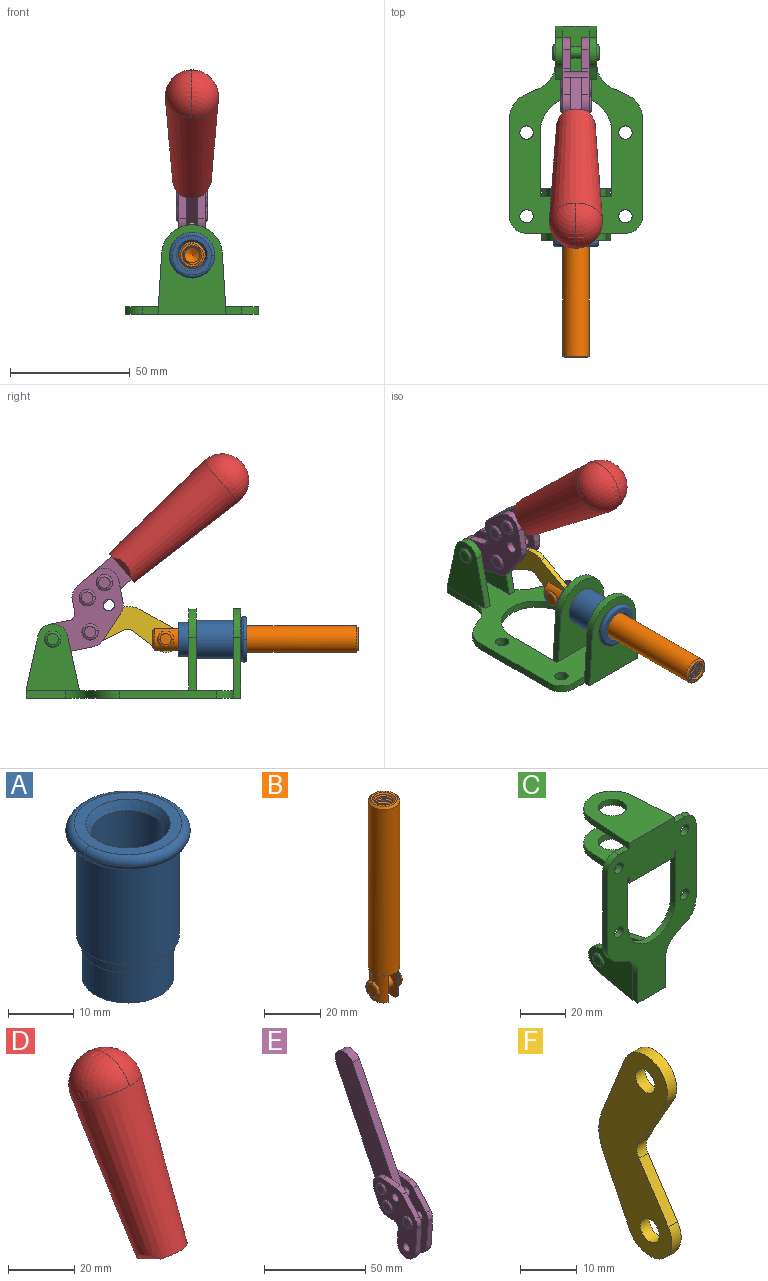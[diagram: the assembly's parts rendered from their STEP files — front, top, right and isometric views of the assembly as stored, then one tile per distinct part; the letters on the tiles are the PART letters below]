
ASSEMBLY  parts=6 mates=6
PART A: 15 faces, bbox 20.6x20.6x28.7 mm
  f0: torus R=8.26mm, axis (0,0,1), area 56.8mm2, adj f1,f10,f12
  f1: torus R=8.26mm, axis (0,0,1), area 56.8mm2, adj f0,f6,f13
  f2: cylinder r=5.59mm len=25.91mm, axis (0,0,1), area 909.6mm2, adj f3,f4
  f3: cone r=6.86mm half-angle=45deg, axis (0,0,-1), area 70.2mm2, adj f2,f14
  f4: cone r=6.47mm half-angle=30deg, axis (0,0,1), area 66.7mm2, adj f2,f13
  f5: cylinder r=7.04mm len=14.07mm, axis (0,0,1), area 252.6mm2, adj f11,f14
  f6: torus R=8.26mm, axis (0,0,1), area 56.8mm2, adj f1,f12,f13
  f7: cylinder r=7.16mm len=14.33mm, axis (0,0,1), area 91.5mm2, adj f9,f11
  f8: cylinder r=7.86mm len=18.42mm, axis (0,0,1), area 909.6mm2, adj f9,f10
  f9: plane 15.72x15.72mm, normal (0,0,-1), area 33mm2, adj f7,f8
  f10: plane 16.51x16.51mm, normal (0,0,-1), area 19.9mm2, adj f0,f8,f12
  f11: plane 14.33x14.33mm, normal (0,0,-1), area 5.7mm2, adj f5,f7
  f12: torus R=8.26mm, axis (0,0,1), area 56.8mm2, adj f0,f6,f10
  f13: plane 16.51x16.51mm, normal (0,0,1), area 82.7mm2, adj f1,f4,f6
  f14: plane 14.07x14.07mm, normal (0,0,-1), area 7.8mm2, adj f3,f5
PART B: 48 faces, bbox 12.6x11.1x86.1 mm
  f0: torus R=2.41mm, axis (-1,0,0), area 15mm2, adj f30,f32,f34
  f1: torus R=2.41mm, axis (-1,0,0), area 15mm2, adj f29,f31,f33
  f2: cylinder r=5.54mm len=72.39mm, axis (0,0,1), area 2518.5mm2, adj f3,f4,f42,f43
  f3: cone r=5.54mm half-angle=45deg, axis (0,0,1), area 7.6mm2, adj f2,f5,f41
  f4: cone r=5.54mm half-angle=45deg, axis (0,0,-1), area 34.9mm2, adj f2,f39
  f5: cylinder r=5.08mm len=11.48mm, axis (0,0,1), area 108.3mm2, adj f3,f7,f8,f41
  f6: cylinder r=2.41mm len=4.83mm, axis (-1,0,0), area 71.2mm2, adj f40,f41
  f7: cylinder r=2.41mm len=4.83mm, axis (-1,0,0), area 7.6mm2, adj f5,f34
  f8: cone r=5.08mm half-angle=45deg, axis (0,0,1), area 10.6mm2, adj f5,f37,f41
  f9: cone r=3.98mm half-angle=45deg, axis (0,0,1), area 17.6mm2, adj f27,f39,f45,f46,f47
  f10: cylinder r=2.41mm len=4.83mm, axis (-1,0,0), area 7.6mm2, adj f33,f38
  f11: cylinder r=3.2mm len=6.4mm, axis (0,0,1), area 78.4mm2, adj f12,f28,f44,f45,f47
  f12: cylinder r=3.2mm len=6.4mm, axis (0,0,1), area 10.5mm2, adj f11,f13,f45,f47
  f13: cylinder r=3.2mm len=6.4mm, axis (0,0,1), area 10.5mm2, adj f12,f14,f45,f47
  f14: cylinder r=3.2mm len=6.4mm, axis (0,0,1), area 10.5mm2, adj f13,f15,f45,f47
  f15: cylinder r=3.2mm len=6.4mm, axis (0,0,1), area 10.5mm2, adj f14,f16,f45,f47
  f16: cylinder r=3.2mm len=6.4mm, axis (0,0,1), area 10.5mm2, adj f15,f17,f45,f47
  f17: cylinder r=3.2mm len=6.4mm, axis (0,0,1), area 10.5mm2, adj f16,f18,f45,f47
  f18: cylinder r=3.2mm len=6.4mm, axis (0,0,1), area 10.5mm2, adj f17,f19,f45,f47
  f19: cylinder r=3.2mm len=6.4mm, axis (0,0,1), area 10.5mm2, adj f18,f20,f45,f47
  f20: cylinder r=3.2mm len=6.4mm, axis (0,0,1), area 10.5mm2, adj f19,f21,f45,f47
  f21: cylinder r=3.2mm len=6.4mm, axis (0,0,1), area 10.5mm2, adj f20,f22,f45,f47
  f22: cylinder r=3.2mm len=6.4mm, axis (0,0,1), area 10.5mm2, adj f21,f23,f45,f47
  f23: cylinder r=3.2mm len=6.4mm, axis (0,0,1), area 10.5mm2, adj f22,f24,f45,f47
  f24: cylinder r=3.2mm len=6.4mm, axis (0,0,1), area 10.5mm2, adj f23,f25,f45,f47
  f25: cylinder r=3.2mm len=6.4mm, axis (0,0,1), area 10.5mm2, adj f24,f26,f45,f47
  f26: cylinder r=3.2mm len=6.4mm, axis (0,0,1), area 10.5mm2, adj f25,f27,f45,f47
  f27: cylinder r=3.2mm len=6.4mm, axis (0,0,1), area 7.4mm2, adj f9,f26,f45,f47
  f28: cone r=3.2mm half-angle=60deg, axis (0,0,1), area 37.2mm2, adj f11
  f29: plane 4.83x4.83mm, normal (-1,0,0), area 18.3mm2, adj f1,f31
  f30: plane 4.83x4.83mm, normal (1,0,0), area 18.3mm2, adj f0,f32
  f31: torus R=2.41mm, axis (-1,0,0), area 15mm2, adj f1,f29,f33
  f32: torus R=2.41mm, axis (-1,0,0), area 15mm2, adj f0,f30,f34
  f33: plane 6.83x6.83mm, normal (1,0,0), area 18.3mm2, adj f1,f10,f31
  f34: plane 6.83x6.83mm, normal (-1,0,0), area 18.3mm2, adj f0,f7,f32
  f35: cone r=5.08mm half-angle=45deg, axis (0,0,1), area 10.6mm2, adj f36,f38,f40
  f36: plane 7.25x1.97mm, normal (0,0,-1), area 10mm2, adj f35,f40
  f37: plane 7.25x1.97mm, normal (0,0,-1), area 10mm2, adj f8,f41
  f38: cylinder r=5.08mm len=11.48mm, axis (0,0,1), area 108.3mm2, adj f10,f35,f40,f42
  f39: plane 9.55x9.55mm, normal (0,0,1), area 22mm2, adj f4,f9
  f40: plane 12.76x10.09mm, normal (1,0,0), area 95.7mm2, adj f6,f35,f36,f38,f42,f43
  f41: plane 12.76x10.09mm, normal (-1,0,0), area 95.7mm2, adj f3,f5,f6,f8,f37,f43
  f42: cone r=5.54mm half-angle=45deg, axis (0,0,1), area 7.6mm2, adj f2,f38,f40
  f43: plane 11.07x4.7mm, normal (0,0,-1), area 50.4mm2, adj f2,f40,f41
  f44: plane 0.89x0.62mm, normal (-1,0,0), area 0.3mm2, adj f11,f45,f46,f47
  f45: bspline ~24.8x7.63mm, area 266.6mm2, adj f9,f11,f12,f13,f14,f15,f16,f17
  f46: bspline ~24.87x7.63mm, area 73.6mm2, adj f9,f44,f45,f47
  f47: bspline ~24.98x7.63mm, area 272.5mm2, adj f9,f11,f12,f13,f14,f15,f16,f17
PART C: 55 faces, bbox 55.7x37.4x89.8 mm
  f0: torus R=2.41mm, axis (-1,0,0), area 15mm2, adj f11,f15,f25
  f1: torus R=2.41mm, axis (-1,0,0), area 15mm2, adj f10,f12,f22
  f2: cylinder r=2.78mm len=5.56mm, axis (0,-1,0), area 54.2mm2, adj f30,f54
  f3: cylinder r=14.99mm len=29.97mm, axis (0,-1,0), area 145.9mm2, adj f30,f49,f53,f54
  f4: cylinder r=2.78mm len=5.56mm, axis (0,-1,0), area 54.2mm2, adj f30,f54
  f5: cylinder r=2.78mm len=5.56mm, axis (0,-1,0), area 54.2mm2, adj f30,f54
  f6: cylinder r=2.78mm len=5.56mm, axis (0,-1,0), area 54.2mm2, adj f30,f54
  f7: cylinder r=6.35mm len=12.7mm, axis (0,0,1), area 123.6mm2, adj f27,f51
  f8: cylinder r=6.35mm len=12.7mm, axis (0,0,-1), area 124.7mm2, adj f21,f35
  f9: cylinder r=2.41mm len=11.18mm, axis (-1,0,0), area 169.4mm2, adj f16,f19
  f10: plane 4.83x4.83mm, normal (1,0,0), area 18.3mm2, adj f1,f12
  f11: plane 4.83x4.83mm, normal (-1,0,0), area 18.3mm2, adj f0,f15
  f12: torus R=2.41mm, axis (-1,0,0), area 15mm2, adj f1,f10,f22
  f13: cylinder r=6.35mm len=12.41mm, axis (1,0,0), area 53.4mm2, adj f18,f19,f22,f23
  f14: cylinder r=6.35mm len=12.41mm, axis (-1,0,0), area 53.4mm2, adj f16,f17,f24,f25
  f15: torus R=2.41mm, axis (-1,0,0), area 15mm2, adj f0,f11,f25
  f16: plane 27.86x22.35mm, normal (1,0,0), area 425.4mm2, adj f9,f14,f17,f24,f30
  f17: plane 22.86x4.97mm, normal (0,0.21,0.98), area 72.5mm2, adj f14,f16,f25,f30
  f18: plane 22.86x4.97mm, normal (0,0.21,0.98), area 72.5mm2, adj f13,f19,f22,f30
  f19: plane 27.86x22.35mm, normal (-1,0,0), area 425.4mm2, adj f9,f13,f18,f23,f30
  f20: cylinder r=12.7mm len=25.35mm, axis (0,0,-1), area 119.8mm2, adj f21,f34,f35,f36
  f21: plane 34.21x28.07mm, normal (0,0,-1), area 702.4mm2, adj f8,f20,f30,f34,f36
  f22: plane 27.96x22.45mm, normal (1,0,0), area 407.2mm2, adj f1,f12,f13,f18,f23,f30,f42,f43
  f23: plane 22.86x4.97mm, normal (0,0.21,-0.98), area 72.5mm2, adj f13,f19,f22,f44
  f24: plane 22.86x4.97mm, normal (0,0.21,-0.98), area 72.5mm2, adj f14,f16,f25,f44
  f25: plane 27.86x22.35mm, normal (-1,0,0), area 407.1mm2, adj f0,f14,f15,f17,f24,f30,f45,f46
  f26: plane 3.1x0.95mm, normal (0,0,-1), area 2.7mm2, adj f30,f49,f50,f54
  f27: plane 34.21x28.07mm, normal (0,0,1), area 702.4mm2, adj f7,f28,f30,f50,f52
  f28: cylinder r=12.7mm len=25.35mm, axis (0,0,1), area 118.8mm2, adj f27,f50,f51,f52
  f29: plane 3.1x0.95mm, normal (0,0,-1), area 2.7mm2, adj f30,f52,f53,f54
  f30: plane 86.54x55.63mm, normal (0,1,0), area 2362.9mm2, adj f2,f3,f4,f5,f6,f16,f17,f18
  f31: plane 40.56x3.1mm, normal (-1,0,0), area 125.7mm2, adj f30,f32,f48,f54
  f32: cylinder r=7.11mm len=7.11mm, axis (0,-1,0), area 34.6mm2, adj f30,f31,f33,f54
  f33: plane 6.67x3.1mm, normal (0,0,1), area 20.4mm2, adj f30,f32,f34,f54
  f34: plane 25.39x3.13mm, normal (-1,0.06,0), area 79.5mm2, adj f20,f21,f33,f35,f54
  f35: plane 37.31x28.45mm, normal (0,0,1), area 789.9mm2, adj f8,f20,f34,f36,f54
  f36: plane 25.39x3.13mm, normal (1,0.06,0), area 79.5mm2, adj f20,f21,f35,f37,f54
  f37: plane 6.67x3.1mm, normal (0,0,1), area 20.4mm2, adj f30,f36,f38,f54
  f38: cylinder r=7.11mm len=7.11mm, axis (0,-1,0), area 34.6mm2, adj f30,f37,f39,f54
  f39: plane 40.56x3.1mm, normal (1,0,0), area 125.7mm2, adj f30,f38,f40,f54
  f40: cylinder r=11.18mm len=10.16mm, axis (0,-1,0), area 39.5mm2, adj f30,f39,f41,f54
  f41: plane 6.09x3.1mm, normal (0.42,0,-0.91), area 20.8mm2, adj f30,f40,f42,f54
  f42: cylinder r=11.18mm len=9.41mm, axis (0,-1,0), area 37.2mm2, adj f22,f30,f41,f43,f54
  f43: plane 16.5x3.1mm, normal (1,0,0), area 51.1mm2, adj f22,f42,f44,f54
  f44: plane 17.37x3.1mm, normal (0,0,-1), area 53.8mm2, adj f23,f24,f30,f43,f45,f54
  f45: plane 16.5x3.1mm, normal (-1,0,0), area 51.1mm2, adj f25,f44,f46,f54
  f46: cylinder r=11.18mm len=9.41mm, axis (0,-1,0), area 37.2mm2, adj f25,f30,f45,f47,f54
  f47: plane 6.09x3.1mm, normal (-0.42,0,-0.91), area 20.8mm2, adj f30,f46,f48,f54
  f48: cylinder r=11.18mm len=10.16mm, axis (0,-1,0), area 39.5mm2, adj f30,f31,f47,f54
  f49: plane 26.54x3.1mm, normal (-1,0,0), area 82.3mm2, adj f3,f26,f30,f54
  f50: plane 25.39x3.1mm, normal (1,0.06,0), area 78.8mm2, adj f26,f27,f28,f51,f54
  f51: plane 37.31x28.45mm, normal (0,0,-1), area 789.9mm2, adj f7,f28,f50,f52,f54
  f52: plane 25.39x3.1mm, normal (-1,0.06,0), area 78.8mm2, adj f27,f28,f29,f51,f54
  f53: plane 26.54x3.1mm, normal (1,0,0), area 82.3mm2, adj f3,f29,f30,f54
  f54: plane 89.66x55.63mm, normal (0,-1,0), area 2678.5mm2, adj f2,f3,f4,f5,f6,f26,f29,f31
PART D: 11 faces, bbox 22.3x42.6x64.5 mm
  f0: sphere r=11.13mm, area 411.4mm2, adj f1,f8
  f1: cone r=11.11mm half-angle=3.3deg, axis (0,0.44,0.9), area 3251.8mm2, adj f0,f7,f8,f9,f10
  f2: cylinder r=6.16mm len=11.7mm, axis (1,0,0), area 89.5mm2, adj f3,f4,f5,f6
  f3: plane 60.23x36.75mm, normal (-1,0,0), area 763.6mm2, adj f2,f4,f6,f10
  f4: plane 51.37x25.05mm, normal (0,0.9,-0.44), area 264.2mm2, adj f2,f3,f5,f10
  f5: plane 60.23x36.75mm, normal (1,0,0), area 763.6mm2, adj f2,f4,f6,f10
  f6: plane 51.37x25.05mm, normal (0,-0.9,0.44), area 264.2mm2, adj f2,f3,f5,f10
  f7: plane 9.95x5.95mm, normal (0.71,-0.31,-0.64), area 25.8mm2, adj f1,f10
  f8: sphere r=11.13mm, area 411.4mm2, adj f0,f1
  f9: plane 9.95x5.95mm, normal (-0.71,-0.31,-0.64), area 25.8mm2, adj f1,f10
  f10: plane 14.27x11.38mm, normal (0,-0.44,-0.9), area 106.7mm2, adj f1,f3,f4,f5,f6,f7,f9
PART E: 59 faces, bbox 12.9x60.2x99.6 mm
  f0: torus R=2.39mm, axis (-1,0,0), area 14.9mm2, adj f20,f43,f51
  f1: torus R=2.39mm, axis (-1,0,0), area 14.9mm2, adj f19,f42,f51
  f2: torus R=2.39mm, axis (-1,0,0), area 14.9mm2, adj f18,f35,f51
  f3: torus R=2.39mm, axis (-1,0,0), area 14.9mm2, adj f14,f17,f23
  f4: torus R=2.39mm, axis (-1,0,0), area 14.9mm2, adj f13,f16,f23
  f5: torus R=2.39mm, axis (-1,0,0), area 14.9mm2, adj f12,f15,f23
  f6: cylinder r=2.39mm len=4.78mm, axis (1,0,0), area 46.5mm2, adj f48,f50,f51
  f7: cylinder r=2.39mm len=4.78mm, axis (1,0,0), area 46.5mm2, adj f50,f51
  f8: cylinder r=6.35mm len=12.68mm, axis (1,0,0), area 61.8mm2, adj f38,f39,f50,f51
  f9: cylinder r=2.39mm len=4.78mm, axis (-1,0,0), area 70.5mm2, adj f46,f50
  f10: cylinder r=2.39mm len=4.78mm, axis (-1,0,0), area 46.5mm2, adj f23,f45,f46
  f11: cylinder r=2.39mm len=4.78mm, axis (-1,0,0), area 46.5mm2, adj f23,f46
  f12: plane 4.78x4.78mm, normal (1,0,0), area 17.9mm2, adj f5,f15
  f13: plane 4.78x4.78mm, normal (1,0,0), area 17.9mm2, adj f4,f16
  f14: plane 4.78x4.78mm, normal (1,0,0), area 17.9mm2, adj f3,f17
  f15: torus R=2.39mm, axis (-1,0,0), area 14.9mm2, adj f5,f12,f23
  f16: torus R=2.39mm, axis (-1,0,0), area 14.9mm2, adj f4,f13,f23
  f17: torus R=2.39mm, axis (-1,0,0), area 14.9mm2, adj f3,f14,f23
  f18: plane 4.78x4.78mm, normal (-1,0,0), area 17.9mm2, adj f2,f35
  f19: plane 4.78x4.78mm, normal (-1,0,0), area 17.9mm2, adj f1,f42
  f20: plane 4.78x4.78mm, normal (-1,0,0), area 17.9mm2, adj f0,f43
  f21: plane 2.26x0.2mm, normal (1,0,0), area 0.2mm2, adj f31,f44
  f22: plane 2.26x0.2mm, normal (-1,0,0), area 0.2mm2, adj f41,f44
  f23: plane 39.37x30.77mm, normal (1,0,0), area 565.5mm2, adj f3,f4,f5,f10,f11,f15,f16,f17
  f24: cylinder r=6.1mm len=4.15mm, axis (-1,0,0), area 14.7mm2, adj f23,f25,f32,f46
  f25: plane 10.25x9.01mm, normal (0,-0.75,0.66), area 42.3mm2, adj f23,f24,f26,f46
  f26: cylinder r=6.35mm len=4.64mm, axis (-1,0,0), area 15.6mm2, adj f23,f25,f27,f46
  f27: plane 15.84x3.1mm, normal (0,-1,-0.07), area 49.2mm2, adj f23,f26,f28,f46
  f28: cylinder r=6.35mm len=12.68mm, axis (-1,0,0), area 61.8mm2, adj f23,f27,f29,f46
  f29: plane 8.11x3.1mm, normal (0,1,0.07), area 25.2mm2, adj f23,f28,f30,f46
  f30: cylinder r=3.05mm len=3.25mm, axis (-1,0,0), area 14.8mm2, adj f23,f29,f31,f46
  f31: plane 5.99x3.1mm, normal (0,0.07,-1), area 18.6mm2, adj f21,f23,f30,f44,f46
  f32: plane 9.5x3.1mm, normal (0,-0.07,1), area 29.5mm2, adj f23,f24,f33,f46,f47
  f33: cylinder r=6.1mm len=8.63mm, axis (-1,0,0), area 39.1mm2, adj f23,f32,f34,f47
  f34: plane 8.65x3.96mm, normal (0,0.91,-0.42), area 29.5mm2, adj f23,f33,f44,f47
  f35: torus R=2.39mm, axis (-1,0,0), area 14.9mm2, adj f2,f18,f51
  f36: plane 10.25x9.01mm, normal (0,-0.75,0.66), area 42.3mm2, adj f37,f49,f50,f51
  f37: cylinder r=6.35mm len=4.64mm, axis (1,0,0), area 15.6mm2, adj f36,f38,f50,f51
  f38: plane 15.84x3.1mm, normal (0,-1,-0.07), area 49.2mm2, adj f8,f37,f50,f51
  f39: plane 8.11x3.1mm, normal (0,1,0.07), area 25.2mm2, adj f8,f40,f50,f51
  f40: cylinder r=3.05mm len=3.25mm, axis (1,0,0), area 14.8mm2, adj f39,f41,f50,f51
  f41: plane 5.99x3.1mm, normal (0,0.07,-1), area 18.6mm2, adj f22,f40,f44,f50,f51
  f42: torus R=2.39mm, axis (-1,0,0), area 14.9mm2, adj f1,f19,f51
  f43: torus R=2.39mm, axis (-1,0,0), area 14.9mm2, adj f0,f20,f51
  f44: cylinder r=6.35mm len=12.12mm, axis (-1,0,0), area 128.9mm2, adj f21,f22,f23,f31,f34,f41,f46,f47
  f45: plane 2.65x1.35mm, normal (1,0,0), area 1mm2, adj f10,f55
  f46: plane 39.08x20.42mm, normal (-1,0,0), area 412.5mm2, adj f9,f10,f11,f24,f25,f26,f27,f28
  f47: plane 77.62x39.82mm, normal (1,0,0), area 850mm2, adj f32,f33,f34,f44,f53,f54,f55
  f48: plane 2.65x1.35mm, normal (-1,0,0), area 1mm2, adj f6,f55
  f49: cylinder r=6.1mm len=4.15mm, axis (1,0,0), area 14.7mm2, adj f36,f50,f51,f56
  f50: plane 39.08x20.42mm, normal (1,0,0), area 412.5mm2, adj f6,f7,f8,f9,f36,f37,f38,f39
  f51: plane 39.37x30.77mm, normal (-1,0,0), area 565.5mm2, adj f0,f1,f2,f6,f7,f8,f35,f36
  f52: plane 8.65x3.96mm, normal (0,0.91,-0.42), area 29.5mm2, adj f44,f51,f57,f58
  f53: plane 68.49x33.4mm, normal (0,0.9,-0.44), area 358.1mm2, adj f44,f47,f54,f58
  f54: cylinder r=6.35mm len=12.06mm, axis (1,0,0), area 93.7mm2, adj f47,f53,f55,f58
  f55: plane 68.49x33.4mm, normal (0,-0.9,0.44), area 358.1mm2, adj f44,f45,f46,f47,f48,f50,f54,f58
  f56: plane 9.5x3.1mm, normal (0,-0.07,1), area 29.5mm2, adj f49,f50,f51,f57,f58
  f57: cylinder r=6.1mm len=8.63mm, axis (1,0,0), area 39.1mm2, adj f51,f52,f56,f58
  f58: plane 77.62x39.82mm, normal (-1,0,0), area 850mm2, adj f44,f52,f53,f54,f55,f56,f57
PART F: 12 faces, bbox 2.3x18.2x42.8 mm
  f0: cylinder r=2.4mm len=4.8mm, axis (1,0,0), area 34.9mm2, adj f4,f11
  f1: cylinder r=10.41mm len=8.47mm, axis (1,0,0), area 20.2mm2, adj f4,f9,f10,f11
  f2: cylinder r=3.05mm len=3.16mm, axis (1,0,0), area 7.7mm2, adj f4,f6,f7,f11
  f3: cylinder r=2.4mm len=4.8mm, axis (1,0,0), area 34.9mm2, adj f4,f11
  f4: plane 42.81x18.23mm, normal (-1,0,0), area 414.1mm2, adj f0,f1,f2,f3,f5,f6,f7,f8
  f5: cylinder r=5.54mm len=10.67mm, axis (1,0,0), area 41.8mm2, adj f4,f6,f10,f11
  f6: plane 11.66x6.53mm, normal (0,-0.87,-0.49), area 30.9mm2, adj f2,f4,f5,f11
  f7: plane 11.17x7.33mm, normal (0,-0.84,0.55), area 30.9mm2, adj f2,f4,f8,f11
  f8: cylinder r=5.54mm len=10.51mm, axis (1,0,0), area 41.8mm2, adj f4,f7,f9,f11
  f9: plane 13.67x6.67mm, normal (0,0.9,-0.44), area 35.1mm2, adj f1,f4,f8,f11
  f10: plane 14.1x5.7mm, normal (0,0.93,0.37), area 35.1mm2, adj f1,f4,f5,f11
  f11: plane 42.81x18.23mm, normal (1,0,0), area 414.1mm2, adj f0,f1,f2,f3,f5,f6,f7,f8
PLACE A rot(axis=(1,0,0),90deg) t=(0,9.14,0)mm
PLACE B rot(axis=(1,0,0),90deg) t=(0,9.52,0)mm
PLACE C rot(axis=(1,0,0),90deg) t=(0,9.14,0)mm fixed
PLACE D rot(axis=(1,0,0),75deg) t=(-0.04,3.86,9.14)mm
PLACE E rot(axis=(1,0,0),75deg) t=(0,3.86,9.14)mm
PLACE F rot(axis=(1,0,0),97.5deg) t=(0,12.59,2.22)mm
MATE fastened D.f2 <-> E.f54  axis (1,0,0) through (-2.35,-30.66,91.94)mm
MATE slider A.f2 <-> B.f2  axis (0,1,0) through (0,-38.27,24.61)mm
MATE revolute F.f5 <-> B.f6  axis (1,0,0) through (0,-5.96,24.61)mm
MATE fastened C.f7 <-> A.f0  axis (0,-1,0) through (0,-37.25,24.61)mm
MATE revolute E.f7 <-> C.f0  axis (1,0,0) through (0,41.23,24.61)mm
MATE revolute E.f4 <-> F.f3  axis (-1,0,0) through (0,25.65,27.64)mm
